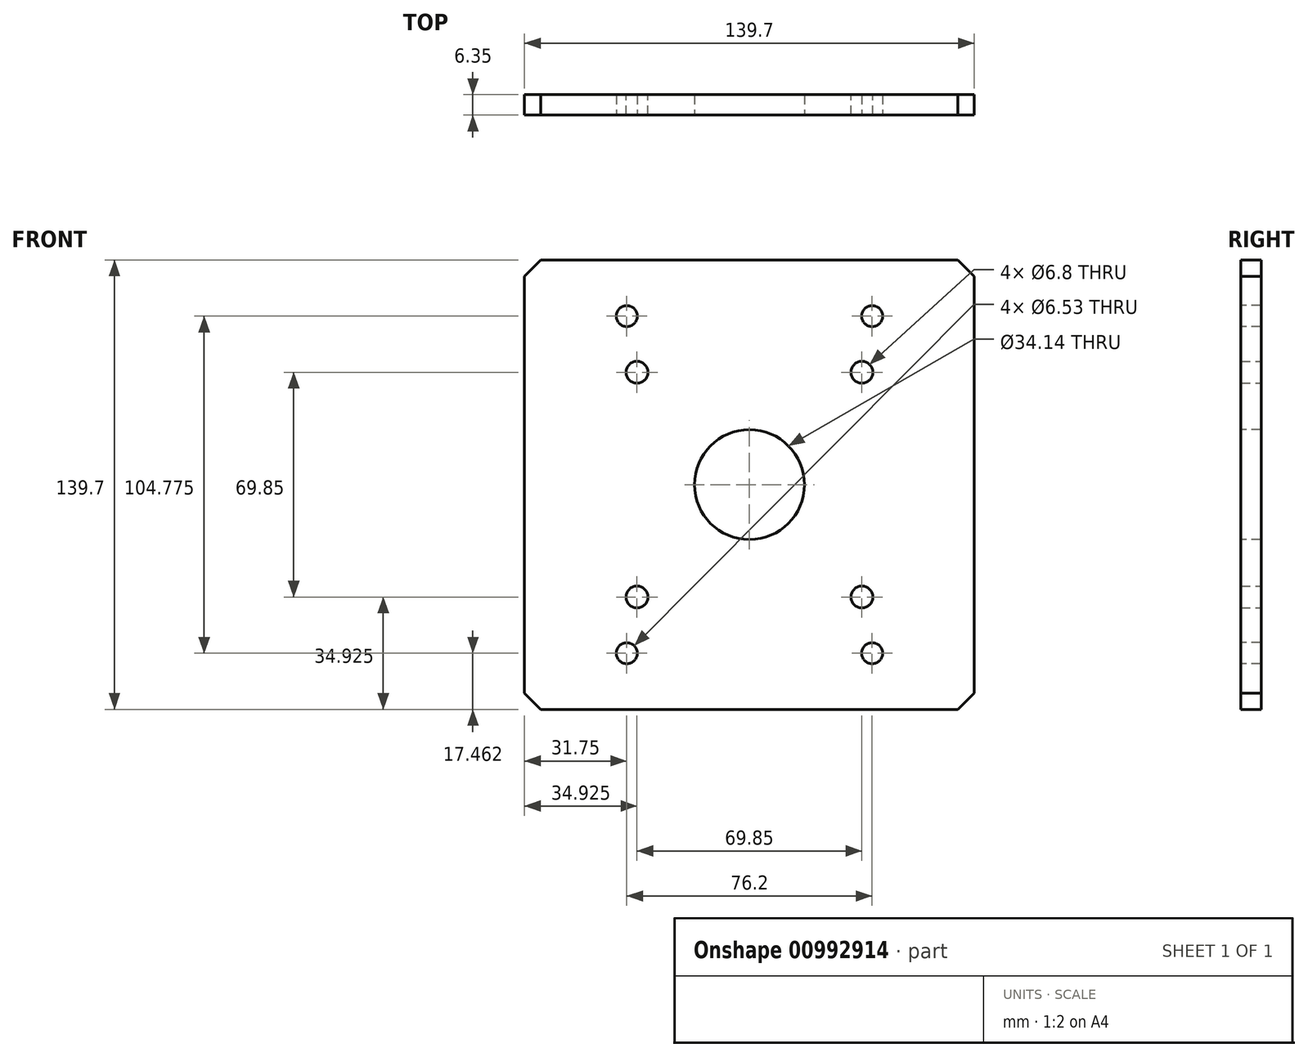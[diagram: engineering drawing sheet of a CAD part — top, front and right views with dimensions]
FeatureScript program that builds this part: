
annotation { "Feature Type Name" : "Feature", "Feature Type Description" : "" }
export const myFeature = defineFeature(function(context is Context, id is Id, definition is map)
    precondition{}
    {
        {
            var Q0;
            Q0=qCreatedBy(makeId("Front.planeOp"),FACE);
            var sketch = newSketch(context, id + "F0", { "sketchPlane" : qUnion([Q0])});
            skLineSegment(sketch, "E0.bottom", {"start": v(69.85, 69.85) * mm, "end": v(-69.85, 69.85) * mm});
            skLineSegment(sketch, "E0.top", {"start": v(69.85, -69.85) * mm, "end": v(-69.85, -69.85) * mm});
            skLineSegment(sketch, "E0.left", {"start": v(69.85, 69.85) * mm, "end": v(69.85, -69.85) * mm});
            skLineSegment(sketch, "E0.right", {"start": v(-69.85, 69.85) * mm, "end": v(-69.85, -69.85) * mm});
            skPoint(sketch, "E0.middle", {"position": v(0, 0) * mm});
            skSolve(sketch);
        }
        {
            var Q0;
            Q0 = qSketchRegion(id + "F0", true);
            extrude(context, id + "F1", {"entities" : qUnion([Q0]), "depth" : 6.35 * mm, "offsetDistance" : 25.4 * mm});
        }
        {
            var Q0;
            Q0=makeQuery(id+"F1.opExtrude","CAP_FACE",FACE,{"disambiguationData":[OSD([sQuery(id+"F0.wireOp",EDGE,"E0.bottom"),sQuery(id+"F0.wireOp",EDGE,"E0.top"),sQuery(id+"F0.wireOp",EDGE,"E0.left"),sQuery(id+"F0.wireOp",EDGE,"E0.right")])],"isStart":true});
            var sketch = newSketch(context, id + "F2", { "sketchPlane" : qUnion([Q0])});
            skPoint(sketch, "E1.middle", {"position": v(0, 0) * mm});
            skCircle(sketch, "E2", {"center": v(-34.93, 34.93) * mm, "radius": 4.76 * mm});
            skCircle(sketch, "E3", {"center": v(34.93, 34.93) * mm, "radius": 4.76 * mm});
            skCircle(sketch, "E4", {"center": v(34.93, -34.93) * mm, "radius": 4.76 * mm});
            skCircle(sketch, "E5", {"center": v(-34.93, -34.93) * mm, "radius": 4.76 * mm});
            skSolve(sketch);
        }
        {
            var Q0;
            Q0=makeQuery(id+"F1.opExtrude","SWEPT_EDGE",EDGE,{"disambiguationData":[OSD([sQuery(id+"F0.wireOp",EDGE,"E0.bottom"),sQuery(id+"F0.wireOp",EDGE,"E0.right")])]});
            var Q1;
            Q1=makeQuery(id+"F1.opExtrude","SWEPT_EDGE",EDGE,{"disambiguationData":[OSD([sQuery(id+"F0.wireOp",EDGE,"E0.bottom"),sQuery(id+"F0.wireOp",EDGE,"E0.left")])]});
            var Q2;
            Q2=makeQuery(id+"F1.opExtrude","SWEPT_EDGE",EDGE,{"disambiguationData":[OSD([sQuery(id+"F0.wireOp",EDGE,"E0.top"),sQuery(id+"F0.wireOp",EDGE,"E0.left")])]});
            var Q3;
            Q3=makeQuery(id+"F1.opExtrude","SWEPT_EDGE",EDGE,{"disambiguationData":[OSD([sQuery(id+"F0.wireOp",EDGE,"E0.top"),sQuery(id+"F0.wireOp",EDGE,"E0.right")])]});
            chamfer(context, id + "F3", {"entities" : qUnion([Q0, Q1, Q2, Q3]), "width" : 5.08 * mm, "tangentPropagation" : true});
        }
        {
            var Q0;
            Q0=sQuery(id+"F2.wireOp",VERTEX,"E2.center");
            var Q1;
            Q1=sQuery(id+"F2.wireOp",VERTEX,"E5.center");
            var Q2;
            Q2=sQuery(id+"F2.wireOp",VERTEX,"E4.center");
            var Q3;
            Q3=sQuery(id+"F2.wireOp",VERTEX,"E3.center");
            var Q4;
            Q4=makeQuery(id+"F1.opExtrude","SWEPT_BODY",BODY,{"disambiguationData":[OSD([sQuery(id+"F0.wireOp",EDGE,"E0.bottom"),sQuery(id+"F0.wireOp",EDGE,"E0.top"),sQuery(id+"F0.wireOp",EDGE,"E0.left"),sQuery(id+"F0.wireOp",EDGE,"E0.right")])]});
            hole(context, id + "F4", {"style" : HoleStyle.SIMPLE, "endStyle" : HoleEndStyle.THROUGH, "standardTappedOrClearance" : lookupTablePath({ "standard" : "ISO", "engagement" : "75%", "pitch" : "1.25 mm", "size" : "M8", "type" : "Tapped" }), "standardBlindInLast" : lookupTablePath({ "standard" : "ISO", "fit" : "Normal", "engagement" : "75%", "pitch" : "1.25 mm", "size" : "M8", "type" : "Clearance & tapped" }), "holeDiameter" : 6.8 * mm, "majorDiameter" : 8 * mm, "showTappedDepth" : true, "isTappedThrough" : true, "tappedDepth" : 12.7 * mm, "tapClearance" : 3, "locations" : qUnion([Q0, Q1, Q2, Q3]), "scope" : qUnion([Q4])});
        }
        {
            var Q0;
            Q0=makeQuery(id+"F1.opExtrude","CAP_FACE",FACE,{"disambiguationData":[OSD([sQuery(id+"F0.wireOp",EDGE,"E0.bottom"),sQuery(id+"F0.wireOp",EDGE,"E0.top"),sQuery(id+"F0.wireOp",EDGE,"E0.left"),sQuery(id+"F0.wireOp",EDGE,"E0.right")])],"isStart":false});
            var sketch = newSketch(context, id + "F5", { "sketchPlane" : qUnion([Q0])});
            skPoint(sketch, "E6.middle", {"position": v(0, 0) * mm});
            skPoint(sketch, "E7", {"position": v(38.1, -52.39) * mm});
            skPoint(sketch, "E8", {"position": v(-38.1, -52.39) * mm});
            skPoint(sketch, "E9", {"position": v(-38.1, 52.39) * mm});
            skPoint(sketch, "E10", {"position": v(38.1, 52.39) * mm});
            skSolve(sketch);
        }
        {
            var Q0;
            Q0=sQuery(id+"F5.wireOp",VERTEX,"E10");
            var Q1;
            Q1=sQuery(id+"F5.wireOp",VERTEX,"E9");
            var Q2;
            Q2=sQuery(id+"F5.wireOp",VERTEX,"E8");
            var Q3;
            Q3=sQuery(id+"F5.wireOp",VERTEX,"E7");
            var Q4;
            Q4=makeQuery(id+"F1.opExtrude","SWEPT_BODY",BODY,{"disambiguationData":[OSD([sQuery(id+"F0.wireOp",EDGE,"E0.bottom"),sQuery(id+"F0.wireOp",EDGE,"E0.top"),sQuery(id+"F0.wireOp",EDGE,"E0.left"),sQuery(id+"F0.wireOp",EDGE,"E0.right")])]});
            hole(context, id + "F6", {"style" : HoleStyle.SIMPLE, "endStyle" : HoleEndStyle.THROUGH, "standardTappedOrClearance" : lookupTablePath({ "standard" : "ANSI", "engagement" : "75%", "pitch" : "18 tpi", "size" : "5/16", "type" : "Tapped" }), "standardBlindInLast" : lookupTablePath({ "standard" : "ANSI", "fit" : "Normal", "engagement" : "75%", "pitch" : "18 tpi", "size" : "5/16", "type" : "Clearance & tapped" }), "holeDiameter" : 6.53 * mm, "majorDiameter" : 7.94 * mm, "showTappedDepth" : true, "isTappedThrough" : true, "tappedDepth" : 12.7 * mm, "tapClearance" : 3, "locations" : qUnion([Q0, Q1, Q2, Q3]), "scope" : qUnion([Q4])});
        }
        {
            var Q0;
            Q0=makeQuery(id+"F1.opExtrude","CAP_FACE",FACE,{"disambiguationData":[OSD([sQuery(id+"F0.wireOp",EDGE,"E0.bottom"),sQuery(id+"F0.wireOp",EDGE,"E0.top"),sQuery(id+"F0.wireOp",EDGE,"E0.left"),sQuery(id+"F0.wireOp",EDGE,"E0.right")])],"isStart":false});
            var sketch = newSketch(context, id + "F7", { "sketchPlane" : qUnion([Q0])});
            skPoint(sketch, "E11", {"position": v(0, 0) * mm});
            skSolve(sketch);
        }
        {
            var Q0;
            Q0=sQuery(id+"F7.wireOp",VERTEX,"E11");
            var Q1;
            Q1=makeQuery(id+"F1.opExtrude","SWEPT_BODY",BODY,{"disambiguationData":[OSD([sQuery(id+"F0.wireOp",EDGE,"E0.bottom"),sQuery(id+"F0.wireOp",EDGE,"E0.top"),sQuery(id+"F0.wireOp",EDGE,"E0.left"),sQuery(id+"F0.wireOp",EDGE,"E0.right")])]});
            hole(context, id + "F8", {"style" : HoleStyle.SIMPLE, "endStyle" : HoleEndStyle.THROUGH, "standardTappedOrClearance" : lookupTablePath({ "fit" : "Normal (ASME)", "standard" : "ANSI", "size" : "1 1/4", "type" : "Clearance" }), "standardBlindInLast" : lookupTablePath({ "fit" : "Normal", "standard" : "ANSI", "engagement" : "75%", "pitch" : "7 tpi", "size" : "1 1/4", "type" : "Clearance & tapped" }), "holeDiameter" : 34.14 * mm, "majorDiameter" : 6.35 * mm, "isTappedThrough" : true, "tappedDepth" : 12.7 * mm, "tapClearance" : 3, "locations" : qUnion([Q0]), "scope" : qUnion([Q1])});
        }
    });
